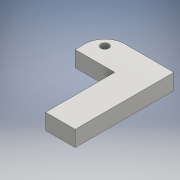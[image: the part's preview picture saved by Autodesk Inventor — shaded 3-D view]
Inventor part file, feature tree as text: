
AUTODESK INVENTOR PART (.ipt)
format: ipt  version: 2016 (Build 200138000, 138)  size: 111,616 bytes
history: native  units: mm
features: sketch x3, extrude x2, fillet x1, hole x1
ambient origin geometry x8: Origin, YZ Plane, XZ Plane, XY Plane, X Axis, Y Axis, Z Axis, Center Point
bodies: Body1 (feature_tree)
feature tree (7):
  extrude  "Extrusion2"  Depth=8.0mm
  extrude  "Extrusion3"  Depth=15.0mm
  fillet  "Fillet1"  Radius=20.0mm
  hole  "Hole1"  [1 undecoded]
  sketch  "Sketch2"  dims[d5=15.0mm d6=8.0mm]
  sketch  "Sketch3"  dims[d7=50.0mm d8=0.0mm d9=15.0mm d10=20.0mm d11=0.0mm]
  sketch  "Sketch5"  dims[d12=10.0mm d13=6.0mm d14=6.0mm d15=4.0mm d16=6.0mm d17=4.0mm d18=2.0mm d19=90.0deg d20=8.0mm d21=20.594885mm]
note: 1 required parameter value undecoded (feature->parameter linkage not recoverable at this tier; creation-order binding heuristic only, values carry confidence <= 0.55)
